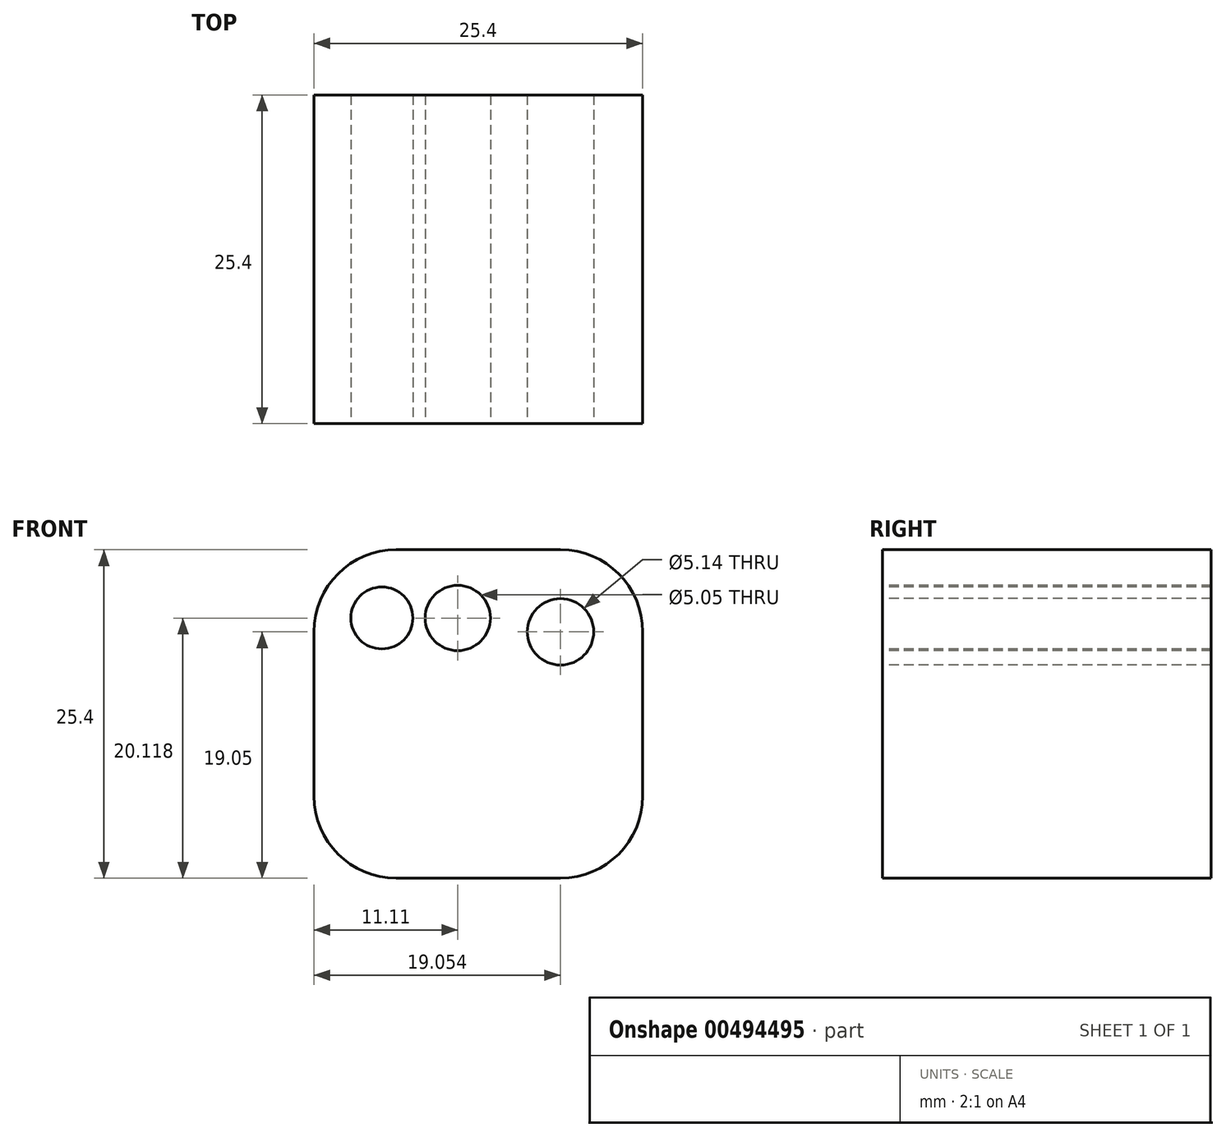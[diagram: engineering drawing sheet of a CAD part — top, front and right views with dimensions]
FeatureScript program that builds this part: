
annotation { "Feature Type Name" : "Feature", "Feature Type Description" : "" }
export const myFeature = defineFeature(function(context is Context, id is Id, definition is map)
    precondition{}
    {
        {
            var Q0;
            Q0=qCreatedBy(makeId("Front.planeOp"),FACE);
            var sketch = newSketch(context, id + "F0", { "sketchPlane" : qUnion([Q0])});
            skLineSegment(sketch, "E0.bottom", {"start": v(-4.76, 14.16) * mm, "end": v(7.94, 14.16) * mm});
            skLineSegment(sketch, "E0.top", {"start": v(-4.76, -11.24) * mm, "end": v(7.94, -11.24) * mm});
            skLineSegment(sketch, "E0.left", {"start": v(-11.1, 7.8) * mm, "end": v(-11.1, -4.9) * mm});
            skLineSegment(sketch, "E0.right", {"start": v(14.3, 7.8) * mm, "end": v(14.3, -4.9) * mm});
            skPoint(sketch, "E1.visualSharp", {"position": v(-11.1, 14.16) * mm});
            skArc(sketch, "E1.filletArc", {"start": v(-4.76, 14.16) * mm, "mid": v(-9.25, 12.3) * mm, "end": v(-11.1, 7.8) * mm});
            skPoint(sketch, "E2.visualSharp", {"position": v(14.3, 14.16) * mm});
            skArc(sketch, "E2.filletArc", {"start": v(14.3, 7.8) * mm, "mid": v(12.43, 12.3) * mm, "end": v(7.94, 14.16) * mm});
            skPoint(sketch, "E3.visualSharp", {"position": v(14.3, -11.24) * mm});
            skArc(sketch, "E3.filletArc", {"start": v(7.94, -11.24) * mm, "mid": v(12.43, -9.38) * mm, "end": v(14.3, -4.9) * mm});
            skPoint(sketch, "E4.visualSharp", {"position": v(-11.1, -11.24) * mm});
            skArc(sketch, "E4.filletArc", {"start": v(-11.1, -4.9) * mm, "mid": v(-9.25, -9.38) * mm, "end": v(-4.76, -11.24) * mm});
            skSolve(sketch);
        }
        {
            var Q0;
            Q0 = qSketchRegion(id + "F0", true);
            extrude(context, id + "F1", {"entities" : qUnion([Q0]), "depth" : 25.4 * mm});
        }
        {
            var Q0;
            Q0=makeQuery(id+"F1.opExtrude","CAP_FACE",FACE,{"disambiguationData":[OSD([sQuery(id+"F0.wireOp",EDGE,"E0.bottom"),sQuery(id+"F0.wireOp",EDGE,"E0.top"),sQuery(id+"F0.wireOp",EDGE,"E0.left"),sQuery(id+"F0.wireOp",EDGE,"E0.right"),sQuery(id+"F0.wireOp",EDGE,"E1.filletArc"),sQuery(id+"F0.wireOp",EDGE,"E2.filletArc"),sQuery(id+"F0.wireOp",EDGE,"E3.filletArc"),sQuery(id+"F0.wireOp",EDGE,"E4.filletArc")])],"isStart":false});
            var sketch = newSketch(context, id + "F2", { "sketchPlane" : qUnion([Q0])});
            skCircle(sketch, "E5", {"center": v(-5.86, 8.88) * mm, "radius": 2.4 * mm});
            skCircle(sketch, "E6", {"center": v(0, 8.88) * mm, "radius": 2.53 * mm});
            skCircle(sketch, "E7", {"center": v(7.94, 7.8) * mm, "radius": 2.57 * mm});
            skSolve(sketch);
        }
        {
            var Q0;
            Q0 = qSketchRegion(id + "F2", true);
            extrude(context, id + "F3", {"entities" : qUnion([Q0]), "operationType" : NewBodyOperationType.REMOVE, "oppositeDirection" : true, "depth" : 25.4 * mm});
        }
    });
